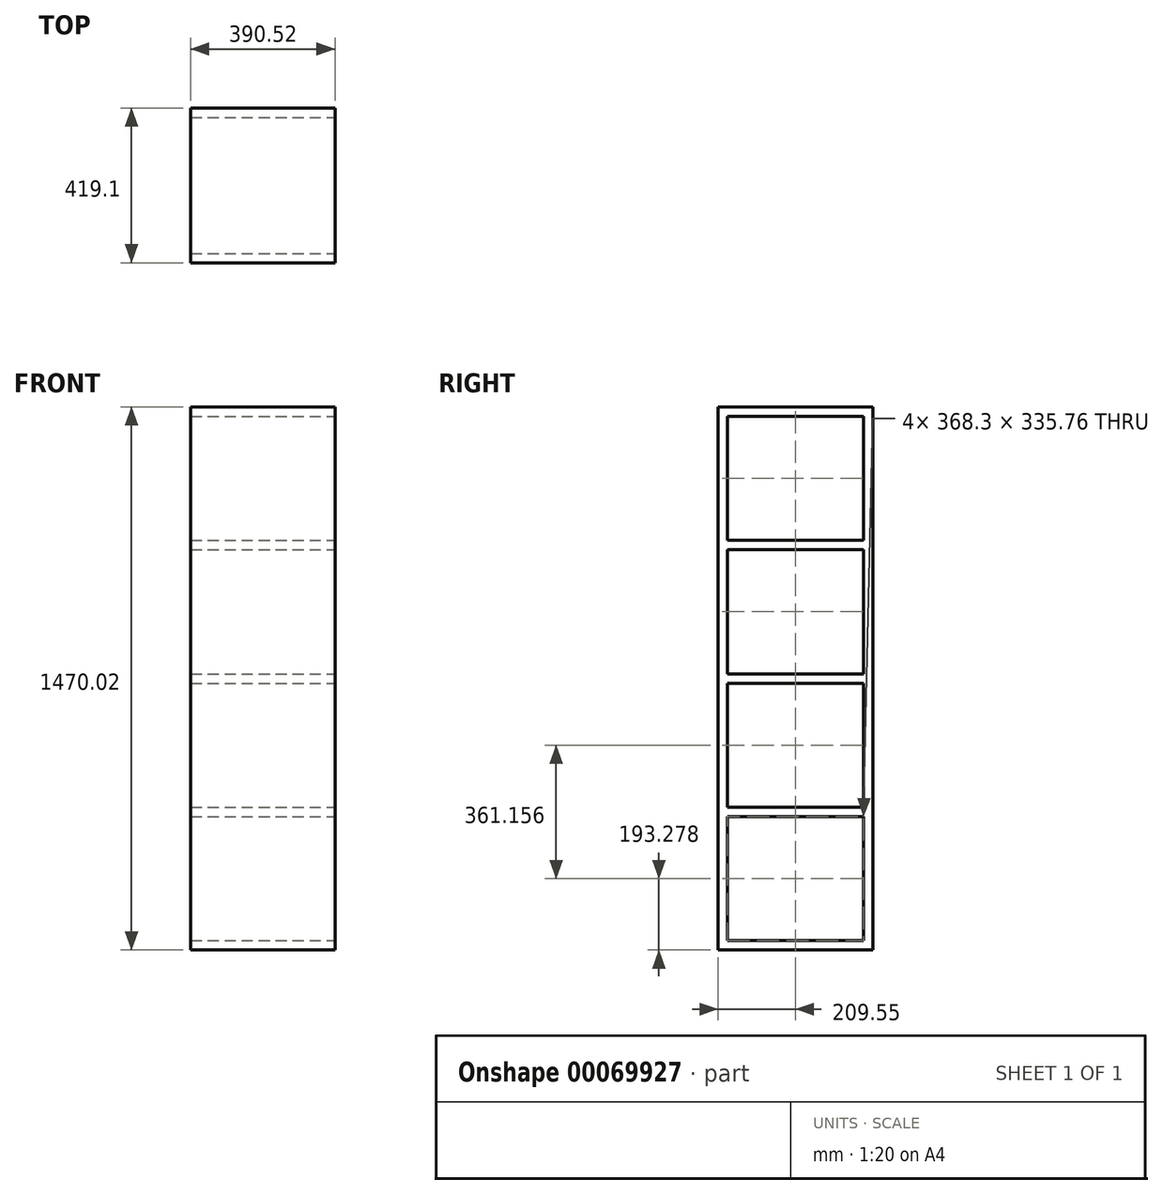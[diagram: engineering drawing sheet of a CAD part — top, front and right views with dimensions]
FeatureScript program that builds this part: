
annotation { "Feature Type Name" : "Feature", "Feature Type Description" : "" }
export const myFeature = defineFeature(function(context is Context, id is Id, definition is map)
    precondition{}
    {
        {
            var Q0;
            Q0=qCreatedBy(makeId("Top.planeOp"),FACE);
            var sketch = newSketch(context, id + "F0", { "sketchPlane" : qUnion([Q0])});
            skLineSegment(sketch, "E0.bottom", {"start": v(195.26, 209.55) * mm, "end": v(-195.26, 209.55) * mm});
            skLineSegment(sketch, "E0.top", {"start": v(195.26, -209.55) * mm, "end": v(-195.26, -209.55) * mm});
            skLineSegment(sketch, "E0.left", {"start": v(195.26, 209.55) * mm, "end": v(195.26, -209.55) * mm});
            skLineSegment(sketch, "E0.right", {"start": v(-195.26, 209.55) * mm, "end": v(-195.26, -209.55) * mm});
            skPoint(sketch, "E0.middle", {"position": v(0, 0) * mm});
            skSolve(sketch);
        }
        {
            var Q0;
            Q0 = qSketchRegion(id + "F0", true);
            extrude(context, id + "F1", {"entities" : qUnion([Q0]), "depth" : 1470.02 * mm});
        }
        {
            var Q0;
            Q0=makeQuery(id+"F1.opExtrude","SWEPT_FACE",FACE,{"disambiguationData":[OSD([sQuery(id+"F0.wireOp",EDGE,"E0.left")])]});
            var sketch = newSketch(context, id + "F2", { "sketchPlane" : qUnion([Q0])});
            skLineSegment(sketch, "E1.bottom", {"start": v(184.15, 25.4) * mm, "end": v(-184.15, 25.4) * mm});
            skLineSegment(sketch, "E1.top", {"start": v(184.15, 361.16) * mm, "end": v(-184.15, 361.16) * mm});
            skLineSegment(sketch, "E1.left", {"start": v(184.15, 25.4) * mm, "end": v(184.15, 361.16) * mm});
            skLineSegment(sketch, "E1.right", {"start": v(-184.15, 25.4) * mm, "end": v(-184.15, 361.16) * mm});
            skPoint(sketch, "E1.middle", {"position": v(0, 193.28) * mm});
            skLineSegment(sketch, "E2.bottom", {"start": v(184.15, 386.56) * mm, "end": v(-184.15, 386.56) * mm});
            skLineSegment(sketch, "E2.top", {"start": v(184.15, 722.31) * mm, "end": v(-184.15, 722.31) * mm});
            skLineSegment(sketch, "E2.left", {"start": v(184.15, 386.56) * mm, "end": v(184.15, 722.31) * mm});
            skLineSegment(sketch, "E2.right", {"start": v(-184.15, 386.56) * mm, "end": v(-184.15, 722.31) * mm});
            skPoint(sketch, "E2.middle", {"position": v(0, 554.43) * mm});
            skLineSegment(sketch, "E3.bottom", {"start": v(184.15, 747.71) * mm, "end": v(-184.15, 747.71) * mm});
            skLineSegment(sketch, "E3.top", {"start": v(184.15, 1083.47) * mm, "end": v(-184.15, 1083.47) * mm});
            skLineSegment(sketch, "E3.left", {"start": v(184.15, 747.71) * mm, "end": v(184.15, 1083.47) * mm});
            skLineSegment(sketch, "E3.right", {"start": v(-184.15, 747.71) * mm, "end": v(-184.15, 1083.47) * mm});
            skPoint(sketch, "E3.middle", {"position": v(0, 915.6) * mm});
            skPoint(sketch, "E3.middle.positionSnap0", {"position": v(0, 722.31) * mm});
            skPoint(sketch, "E3.centerSnap0", {"position": v(0, 722.31) * mm});
            skLineSegment(sketch, "E4.bottom", {"start": v(184.15, 1108.87) * mm, "end": v(-184.15, 1108.87) * mm});
            skLineSegment(sketch, "E4.top", {"start": v(184.15, 1444.62) * mm, "end": v(-184.15, 1444.62) * mm});
            skLineSegment(sketch, "E4.left", {"start": v(184.15, 1108.87) * mm, "end": v(184.15, 1444.63) * mm});
            skLineSegment(sketch, "E4.right", {"start": v(-184.15, 1108.87) * mm, "end": v(-184.15, 1444.62) * mm});
            skPoint(sketch, "E4.middle", {"position": v(0, 1276.75) * mm});
            skLineSegment(sketch, "E5", {"start": v(0, 1470.03) * mm, "end": v(0, 1444.62) * mm});
            skLineSegment(sketch, "E6", {"start": v(0, 1108.87) * mm, "end": v(0, 1083.47) * mm});
            skLineSegment(sketch, "E7", {"start": v(0, 747.71) * mm, "end": v(0, 722.31) * mm});
            skLineSegment(sketch, "E8", {"start": v(0, 386.56) * mm, "end": v(0, 361.16) * mm});
            skLineSegment(sketch, "E9", {"start": v(0, 25.4) * mm, "end": v(0, 0) * mm});
            skLineSegment(sketch, "E10", {"start": v(184.15, 1276.75) * mm, "end": v(209.55, 1276.75) * mm});
            skSolve(sketch);
        }
        {
            var Q0;
            Q0 = qSketchRegion(id + "F2", true);
            extrude(context, id + "F3", {"entities" : qUnion([Q0]), "operationType" : NewBodyOperationType.REMOVE, "endBound" : BoundingType.THROUGH_ALL, "oppositeDirection" : true, "depth" : 25.4 * mm});
        }
    });
